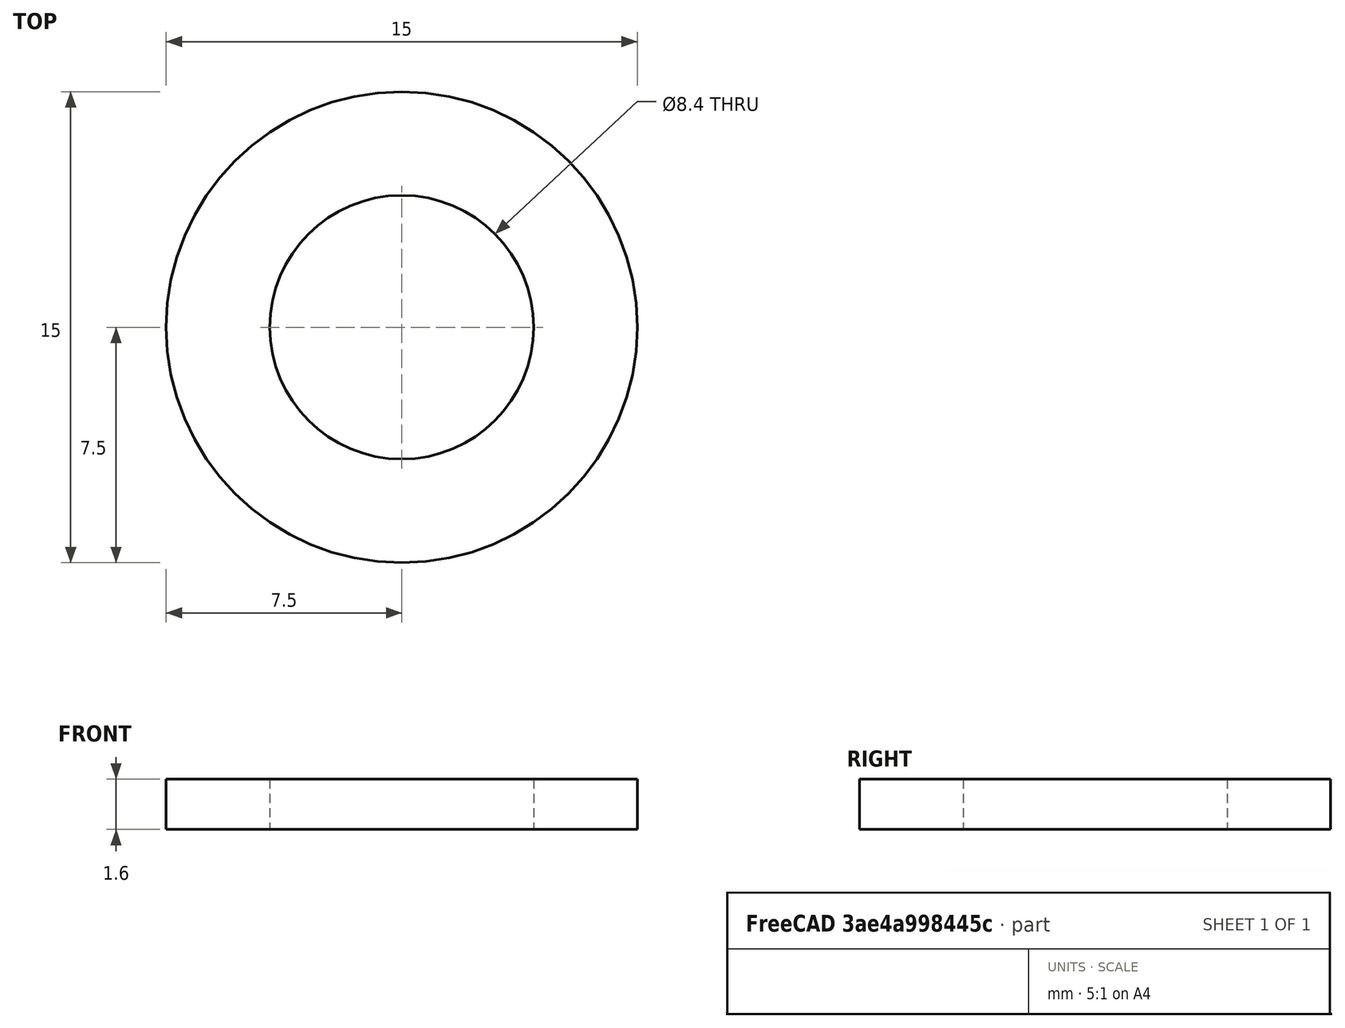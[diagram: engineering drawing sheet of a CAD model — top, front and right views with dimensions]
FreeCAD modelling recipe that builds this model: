
FCSTD DOCUMENT  (FreeCAD 0.14R3700 (Git))
Label: Scheibe DIN 433 - A 8,4
License: CC-BY 3.0
LicenseURL: http://creativecommons.org/licenses/by/3.0/
objects: Sketcher::SketchObject×1, PartDesign::Revolution×1, Part::Feature×1
note: 4 computed .brp shape members not serialized (recipe doc carries the construction recipe); baked Part::Feature solids carry a one-line shape summary decoded from their .brp

FEATURE [Sketcher::SketchObject] Sketch
  Placement = pos=(0,0,0) rot=(0.57735,0.57735,0.57735;2.0944rad)
  sketch-geometry (4):
    g0: LineSegment StartX=4.2 StartY=0 StartZ=0 EndX=7.5 EndY=0 EndZ=0
    g1: LineSegment StartX=7.5 StartY=0 StartZ=0 EndX=7.5 EndY=1.6 EndZ=0
    g2: LineSegment StartX=7.5 StartY=1.6 StartZ=0 EndX=4.2 EndY=1.6 EndZ=0
    g3: LineSegment StartX=4.2 StartY=1.6 StartZ=0 EndX=4.2 EndY=0 EndZ=0
  constraints (12):
    c: Coincident(g0,g1)
    c: Coincident(g1,g2)
    c: Coincident(g2,g3)
    c: Coincident(g3,g0)
    c: Horizontal(g0)
    c: Horizontal(g2)
    c: Vertical(g1)
    c: Vertical(g3)
    c: PointOnObject(g0,g-1)
    c: DistanceY(g1) = 1.6
    c: DistanceX(g-1,g2) = 4.2
    c: DistanceX(g-1,g1) = 7.5
FEATURE [PartDesign::Revolution] Revolution  label="Scheibe DIN 433 - A 8,4 #"
  Angle = 360
  Axis = (0,0,1)
  Base = (0,0,0)
  Placement = pos=(0,0,0) rot=(0.57735,0.57735,0.57735;2.0944rad)
  ReferenceAxis = -> Sketch [V_Axis]
  Reversed = true
  Sketch = -> Sketch
FEATURE [Part::Feature] Revolution001  label="Scheibe DIN 433 - A 8,4 #001"
  Placement = pos=(0,0,0) rot=(0.57735,0.57735,0.57735;2.0944rad)
  shape: bbox 15 x 15 x 1.6 mm, 4 faces (baked)
